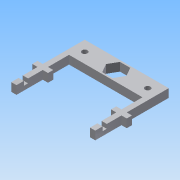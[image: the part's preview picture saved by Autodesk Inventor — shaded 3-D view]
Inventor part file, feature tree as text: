
AUTODESK INVENTOR PART (.ipt)
format: ipt  version: 2015 (Build 190159000, 159)  size: 186,368 bytes
history: native  units: mm
features: extrude x5, sketch x4, projected_geometry x4, reference x2
ambient origin geometry x8: Origin, YZ Plane, XZ Plane, XY Plane, X Axis, Y Axis, Z Axis, Center Point
bodies: Solid1 (feature_tree)
feature tree (15):
  extrude  "Extrusion1"  Depth=20.0mm
  extrude  "Extrusion2"  Depth=10.0mm TaperAngle=0.0deg
  extrude  "Extrusion3"  Depth=60.0mm
  extrude  "Extrusion8"  Depth=14.0mm
  extrude  "Extrusion9"  Depth=40.0mm
  sketch  "Sketch3"  dims[d0=80.0mm d1=20.0mm]
  sketch  "Sketch9"  dims[d2=8.0mm d3=0.0mm d13=10.0mm d14=0.0mm]
  reference  "Reference1"
  reference  "Reference2"
  sketch  "Sketch14"  dims[d40=5.2mm d41=60.0mm]
  projected_geometry  "Projected Loop2"
  sketch  "Sketch15"  dims[d42=10.0mm d43=0.0mm d65=19.5mm d70=40.0mm d73=10.0mm d74=5.0mm d75=50.0mm d78=5.0mm d79=5.0mm d80=5.0mm d81=20.0mm d82=8.0mm d83=0.0mm d84=4.0mm d85=4.0mm d87=8.0mm d88=0.0mm d89=14.0mm]
  projected_geometry  "Projected Loop3"
  projected_geometry  "Projected Loop4"
  projected_geometry  "Projected Loop5"
